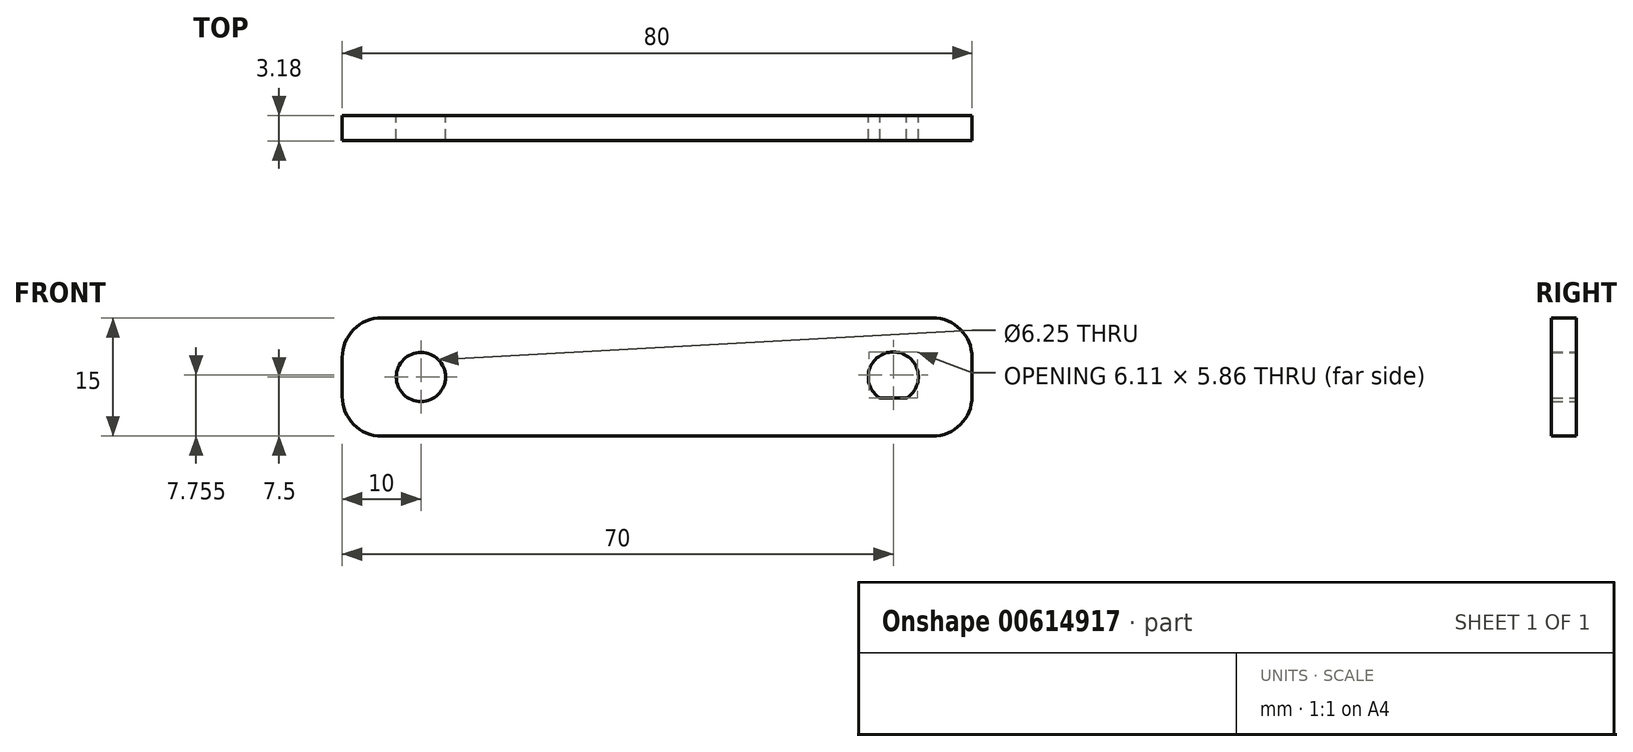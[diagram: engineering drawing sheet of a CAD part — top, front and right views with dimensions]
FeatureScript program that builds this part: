
annotation { "Feature Type Name" : "Feature", "Feature Type Description" : "" }
export const myFeature = defineFeature(function(context is Context, id is Id, definition is map)
    precondition{}
    {
        {
            var Q0;
            Q0=qCreatedBy(makeId("Front.planeOp"),FACE);
            var sketch = newSketch(context, id + "F0", { "sketchPlane" : qUnion([Q0])});
            skLineSegment(sketch, "E0.bottom", {"start": v(35, 7.5) * mm, "end": v(-35, 7.5) * mm});
            skLineSegment(sketch, "E0.top", {"start": v(35, -7.5) * mm, "end": v(-35, -7.5) * mm});
            skLineSegment(sketch, "E0.left", {"start": v(40, 2.5) * mm, "end": v(40, -2.5) * mm});
            skLineSegment(sketch, "E0.right", {"start": v(-40, 2.5) * mm, "end": v(-40, -2.5) * mm});
            skPoint(sketch, "E0.middle", {"position": v(0, 0) * mm});
            skLineSegment(sketch, "E1", {"start": v(0, 0) * mm, "end": v(-30, 0) * mm});
            skCircle(sketch, "E2", {"center": v(-30, 0) * mm, "radius": 3.12 * mm});
            skPoint(sketch, "E3.visualSharp", {"position": v(-40, 7.5) * mm});
            skArc(sketch, "E3.filletArc", {"start": v(-35, 7.5) * mm, "mid": v(-38.54, 6.04) * mm, "end": v(-40, 2.5) * mm});
            skPoint(sketch, "E4.visualSharp", {"position": v(-40, -7.5) * mm});
            skArc(sketch, "E4.filletArc", {"start": v(-40, -2.5) * mm, "mid": v(-38.54, -6.04) * mm, "end": v(-35, -7.5) * mm});
            skPoint(sketch, "E5.visualSharp", {"position": v(40, 7.5) * mm});
            skArc(sketch, "E5.filletArc", {"start": v(40, 2.5) * mm, "mid": v(38.54, 6.04) * mm, "end": v(35, 7.5) * mm});
            skPoint(sketch, "E6.visualSharp", {"position": v(40, -7.5) * mm});
            skArc(sketch, "E6.filletArc", {"start": v(35, -7.5) * mm, "mid": v(38.54, -6.04) * mm, "end": v(40, -2.5) * mm});
            skLineSegment(sketch, "E7", {"start": v(30, 0) * mm, "end": v(0, 0) * mm});
            skLineSegment(sketch, "E8", {"start": v(28.29, -2.67) * mm, "end": v(31.71, -2.67) * mm});
            skArc(sketch, "E9", {"start": v(31.71, -2.67) * mm, "mid": v(30, 3.19) * mm, "end": v(28.29, -2.67) * mm});
            skSolve(sketch);
        }
        {
            var Q0;
            Q0=makeQuery(id+"F0.imprint","IMPRINT",FACE,{"disambiguationData":[TD([[makeQuery(id+"F0.imprint","IMPRINT",EDGE,{"derivedFrom":sQuery(id+"F0.wireOp",EDGE,"E0.bottom")}),1.0]])]});
            extrude(context, id + "F1", {"entities" : qUnion([Q0]), "depth" : 3.17 * mm, "offsetDistance" : 25 * mm});
        }
    });
